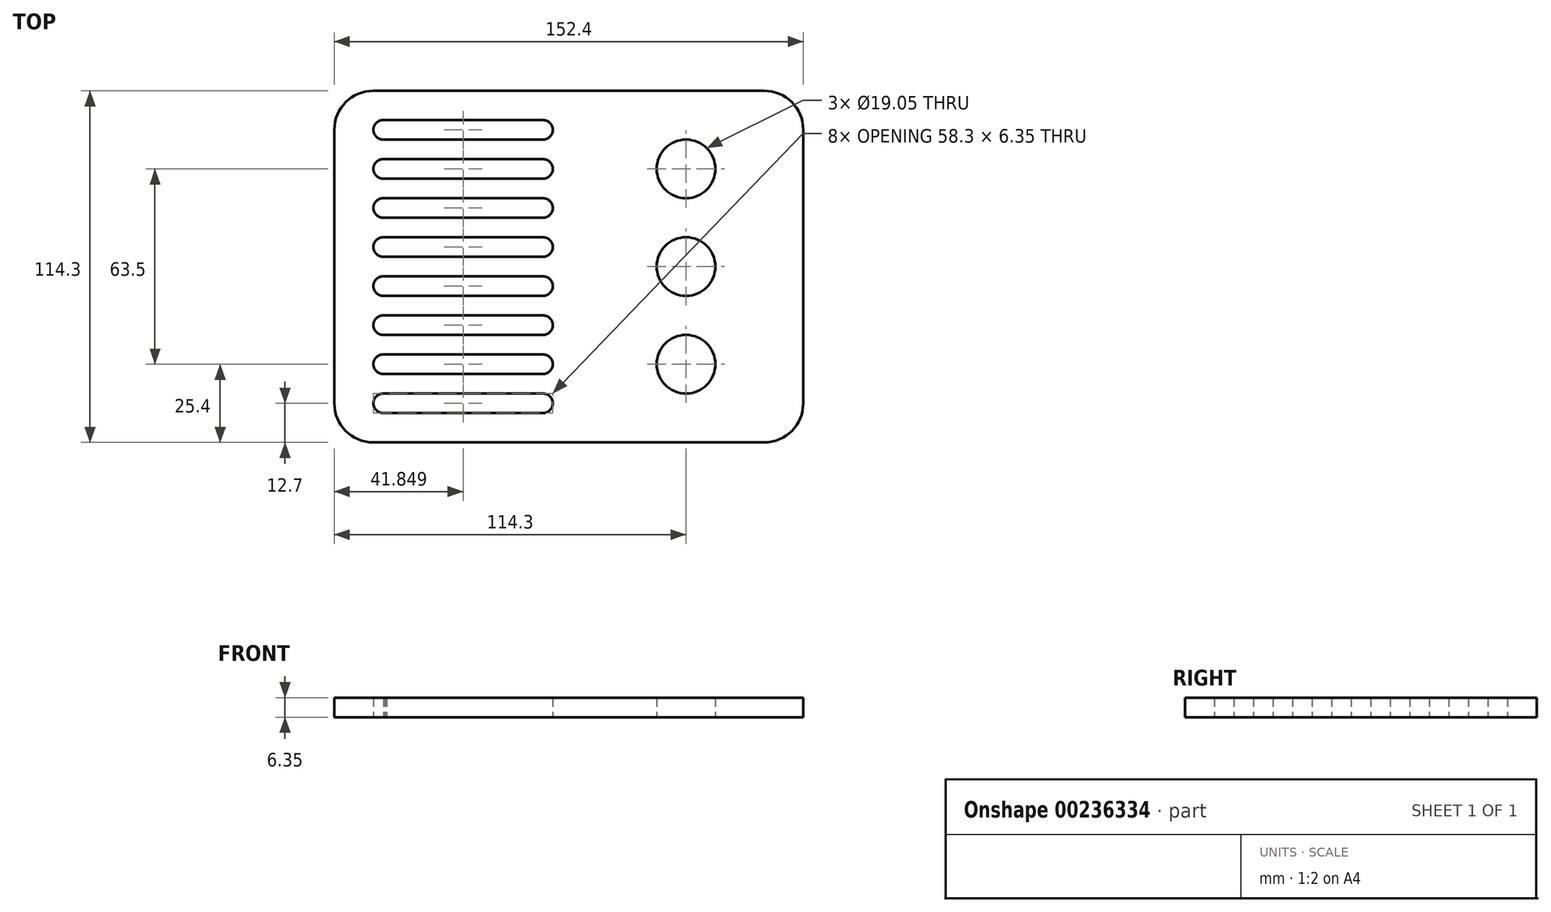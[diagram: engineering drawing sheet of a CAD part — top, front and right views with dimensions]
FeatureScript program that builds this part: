
annotation { "Feature Type Name" : "Feature", "Feature Type Description" : "" }
export const myFeature = defineFeature(function(context is Context, id is Id, definition is map)
    precondition{}
    {
        {
            var Q0;
            Q0=qCreatedBy(makeId("Top.planeOp"),FACE);
            var sketch = newSketch(context, id + "F0", { "sketchPlane" : qUnion([Q0])});
            skLineSegment(sketch, "E0.bottom", {"start": v(76.2, -57.15) * mm, "end": v(-76.2, -57.15) * mm});
            skLineSegment(sketch, "E0.top", {"start": v(76.2, 57.15) * mm, "end": v(-76.2, 57.15) * mm});
            skLineSegment(sketch, "E0.left", {"start": v(76.2, -57.15) * mm, "end": v(76.2, 57.15) * mm});
            skLineSegment(sketch, "E0.right", {"start": v(-76.2, -57.15) * mm, "end": v(-76.2, 57.15) * mm});
            skPoint(sketch, "E0.middle", {"position": v(0, 0) * mm});
            skCircle(sketch, "E1", {"center": v(38.1, -31.75) * mm, "radius": 9.53 * mm});
            skCircle(sketch, "E2", {"center": v(38.1, 0) * mm, "radius": 9.53 * mm});
            skCircle(sketch, "E3", {"center": v(38.1, 31.75) * mm, "radius": 9.53 * mm});
            skArc(sketch, "E4", {"start": v(-9.4, 41.28) * mm, "mid": v(-6.22, 44.45) * mm, "end": v(-9.4, 47.63) * mm});
            skLineSegment(sketch, "E5", {"start": v(-9.4, 47.63) * mm, "end": v(-60.32, 47.63) * mm});
            skLineSegment(sketch, "E6", {"start": v(-9.4, 41.28) * mm, "end": v(-60.2, 41.28) * mm});
            skArc(sketch, "E7", {"start": v(-60.32, 47.63) * mm, "mid": v(-63.5, 44.38) * mm, "end": v(-60.2, 41.28) * mm});
            skLineSegment(sketch, "E8.0.1.0", {"start": v(-9.4, 28.58) * mm, "end": v(-60.2, 28.58) * mm});
            skArc(sketch, "E8.0.1.1", {"start": v(-60.32, 34.93) * mm, "mid": v(-63.5, 31.68) * mm, "end": v(-60.2, 28.58) * mm});
            skLineSegment(sketch, "E8.0.1.2", {"start": v(-9.4, 34.93) * mm, "end": v(-60.32, 34.93) * mm});
            skArc(sketch, "E8.0.1.3", {"start": v(-9.4, 28.58) * mm, "mid": v(-6.22, 31.75) * mm, "end": v(-9.4, 34.93) * mm});
            skLineSegment(sketch, "E8.0.2.0", {"start": v(-9.4, 15.88) * mm, "end": v(-60.2, 15.88) * mm});
            skArc(sketch, "E8.0.2.1", {"start": v(-60.32, 22.23) * mm, "mid": v(-63.5, 18.98) * mm, "end": v(-60.2, 15.88) * mm});
            skLineSegment(sketch, "E8.0.2.2", {"start": v(-9.4, 22.23) * mm, "end": v(-60.32, 22.23) * mm});
            skArc(sketch, "E8.0.2.3", {"start": v(-9.4, 15.88) * mm, "mid": v(-6.22, 19.05) * mm, "end": v(-9.4, 22.23) * mm});
            skLineSegment(sketch, "E8.0.3.0", {"start": v(-9.4, 3.18) * mm, "end": v(-60.2, 3.18) * mm});
            skArc(sketch, "E8.0.3.1", {"start": v(-60.32, 9.53) * mm, "mid": v(-63.5, 6.28) * mm, "end": v(-60.2, 3.18) * mm});
            skLineSegment(sketch, "E8.0.3.2", {"start": v(-9.4, 9.53) * mm, "end": v(-60.32, 9.53) * mm});
            skArc(sketch, "E8.0.3.3", {"start": v(-9.4, 3.18) * mm, "mid": v(-6.22, 6.35) * mm, "end": v(-9.4, 9.53) * mm});
            skLineSegment(sketch, "E8.0.4.0", {"start": v(-9.4, -9.52) * mm, "end": v(-60.2, -9.52) * mm});
            skArc(sketch, "E8.0.4.1", {"start": v(-60.32, -3.17) * mm, "mid": v(-63.5, -6.42) * mm, "end": v(-60.2, -9.52) * mm});
            skLineSegment(sketch, "E8.0.4.2", {"start": v(-9.4, -3.17) * mm, "end": v(-60.32, -3.17) * mm});
            skArc(sketch, "E8.0.4.3", {"start": v(-9.4, -9.52) * mm, "mid": v(-6.22, -6.35) * mm, "end": v(-9.4, -3.17) * mm});
            skLineSegment(sketch, "E8.0.5.0", {"start": v(-9.4, -22.22) * mm, "end": v(-60.2, -22.22) * mm});
            skArc(sketch, "E8.0.5.1", {"start": v(-60.32, -15.87) * mm, "mid": v(-63.5, -19.12) * mm, "end": v(-60.2, -22.22) * mm});
            skLineSegment(sketch, "E8.0.5.2", {"start": v(-9.4, -15.87) * mm, "end": v(-60.32, -15.87) * mm});
            skArc(sketch, "E8.0.5.3", {"start": v(-9.4, -22.22) * mm, "mid": v(-6.22, -19.05) * mm, "end": v(-9.4, -15.87) * mm});
            skLineSegment(sketch, "E8.0.6.0", {"start": v(-9.4, -34.92) * mm, "end": v(-60.2, -34.92) * mm});
            skArc(sketch, "E8.0.6.1", {"start": v(-60.32, -28.57) * mm, "mid": v(-63.5, -31.82) * mm, "end": v(-60.2, -34.92) * mm});
            skLineSegment(sketch, "E8.0.6.2", {"start": v(-9.4, -28.57) * mm, "end": v(-60.32, -28.57) * mm});
            skArc(sketch, "E8.0.6.3", {"start": v(-9.4, -34.92) * mm, "mid": v(-6.22, -31.75) * mm, "end": v(-9.4, -28.57) * mm});
            skLineSegment(sketch, "E8.0.7.0", {"start": v(-9.4, -47.62) * mm, "end": v(-60.2, -47.62) * mm});
            skArc(sketch, "E8.0.7.1", {"start": v(-60.32, -41.27) * mm, "mid": v(-63.5, -44.52) * mm, "end": v(-60.2, -47.62) * mm});
            skLineSegment(sketch, "E8.0.7.2", {"start": v(-9.4, -41.27) * mm, "end": v(-60.32, -41.27) * mm});
            skArc(sketch, "E8.0.7.3", {"start": v(-9.4, -47.62) * mm, "mid": v(-6.22, -44.45) * mm, "end": v(-9.4, -41.27) * mm});
            skLineSegment(sketch, "E8.1.0.0", {"start": v(-8.89, 41.28) * mm, "end": v(-59.69, 41.28) * mm});
            skArc(sketch, "E8.1.0.1", {"start": v(-59.82, 47.63) * mm, "mid": v(-63, 44.38) * mm, "end": v(-59.69, 41.28) * mm});
            skLineSegment(sketch, "E8.1.0.2", {"start": v(-8.89, 47.63) * mm, "end": v(-59.82, 47.63) * mm});
            skArc(sketch, "E8.1.0.3", {"start": v(-8.89, 41.28) * mm, "mid": v(-5.71, 44.45) * mm, "end": v(-8.89, 47.63) * mm});
            skLineSegment(sketch, "E8.1.1.0", {"start": v(-8.89, 28.58) * mm, "end": v(-59.69, 28.58) * mm});
            skArc(sketch, "E8.1.1.1", {"start": v(-59.82, 34.93) * mm, "mid": v(-63, 31.68) * mm, "end": v(-59.69, 28.58) * mm});
            skLineSegment(sketch, "E8.1.1.2", {"start": v(-8.89, 34.93) * mm, "end": v(-59.82, 34.93) * mm});
            skArc(sketch, "E8.1.1.3", {"start": v(-8.89, 28.58) * mm, "mid": v(-5.71, 31.75) * mm, "end": v(-8.89, 34.93) * mm});
            skLineSegment(sketch, "E8.1.2.0", {"start": v(-8.89, 15.88) * mm, "end": v(-59.69, 15.88) * mm});
            skArc(sketch, "E8.1.2.1", {"start": v(-59.82, 22.23) * mm, "mid": v(-63, 18.98) * mm, "end": v(-59.69, 15.88) * mm});
            skLineSegment(sketch, "E8.1.2.2", {"start": v(-8.89, 22.23) * mm, "end": v(-59.82, 22.23) * mm});
            skArc(sketch, "E8.1.2.3", {"start": v(-8.89, 15.88) * mm, "mid": v(-5.71, 19.05) * mm, "end": v(-8.89, 22.23) * mm});
            skLineSegment(sketch, "E8.1.3.0", {"start": v(-8.89, 3.18) * mm, "end": v(-59.69, 3.18) * mm});
            skArc(sketch, "E8.1.3.1", {"start": v(-59.82, 9.53) * mm, "mid": v(-63, 6.28) * mm, "end": v(-59.69, 3.18) * mm});
            skLineSegment(sketch, "E8.1.3.2", {"start": v(-8.89, 9.53) * mm, "end": v(-59.82, 9.53) * mm});
            skArc(sketch, "E8.1.3.3", {"start": v(-8.89, 3.18) * mm, "mid": v(-5.71, 6.35) * mm, "end": v(-8.89, 9.53) * mm});
            skLineSegment(sketch, "E8.1.4.0", {"start": v(-8.89, -9.52) * mm, "end": v(-59.69, -9.52) * mm});
            skArc(sketch, "E8.1.4.1", {"start": v(-59.82, -3.17) * mm, "mid": v(-63, -6.42) * mm, "end": v(-59.69, -9.52) * mm});
            skLineSegment(sketch, "E8.1.4.2", {"start": v(-8.89, -3.17) * mm, "end": v(-59.82, -3.17) * mm});
            skArc(sketch, "E8.1.4.3", {"start": v(-8.89, -9.52) * mm, "mid": v(-5.71, -6.35) * mm, "end": v(-8.89, -3.17) * mm});
            skLineSegment(sketch, "E8.1.5.0", {"start": v(-8.89, -22.22) * mm, "end": v(-59.69, -22.22) * mm});
            skArc(sketch, "E8.1.5.1", {"start": v(-59.82, -15.87) * mm, "mid": v(-63, -19.12) * mm, "end": v(-59.69, -22.22) * mm});
            skLineSegment(sketch, "E8.1.5.2", {"start": v(-8.89, -15.87) * mm, "end": v(-59.82, -15.87) * mm});
            skArc(sketch, "E8.1.5.3", {"start": v(-8.89, -22.22) * mm, "mid": v(-5.71, -19.05) * mm, "end": v(-8.89, -15.87) * mm});
            skLineSegment(sketch, "E8.1.6.0", {"start": v(-8.89, -34.92) * mm, "end": v(-59.69, -34.92) * mm});
            skArc(sketch, "E8.1.6.1", {"start": v(-59.82, -28.57) * mm, "mid": v(-63, -31.82) * mm, "end": v(-59.69, -34.92) * mm});
            skLineSegment(sketch, "E8.1.6.2", {"start": v(-8.89, -28.57) * mm, "end": v(-59.82, -28.57) * mm});
            skArc(sketch, "E8.1.6.3", {"start": v(-8.89, -34.92) * mm, "mid": v(-5.71, -31.75) * mm, "end": v(-8.89, -28.57) * mm});
            skLineSegment(sketch, "E8.1.7.0", {"start": v(-8.89, -47.62) * mm, "end": v(-59.69, -47.62) * mm});
            skArc(sketch, "E8.1.7.1", {"start": v(-59.82, -41.27) * mm, "mid": v(-63, -44.52) * mm, "end": v(-59.69, -47.62) * mm});
            skLineSegment(sketch, "E8.1.7.2", {"start": v(-8.89, -41.27) * mm, "end": v(-59.82, -41.27) * mm});
            skArc(sketch, "E8.1.7.3", {"start": v(-8.89, -47.62) * mm, "mid": v(-5.71, -44.45) * mm, "end": v(-8.89, -41.27) * mm});
            skLineSegment(sketch, "E8.2.0.0", {"start": v(-8.38, 41.28) * mm, "end": v(-59.18, 41.28) * mm});
            skArc(sketch, "E8.2.0.1", {"start": v(-59.3, 47.63) * mm, "mid": v(-62.48, 44.38) * mm, "end": v(-59.18, 41.28) * mm});
            skLineSegment(sketch, "E8.2.0.2", {"start": v(-8.38, 47.63) * mm, "end": v(-59.3, 47.63) * mm});
            skArc(sketch, "E8.2.0.3", {"start": v(-8.38, 41.28) * mm, "mid": v(-5.2, 44.45) * mm, "end": v(-8.38, 47.63) * mm});
            skLineSegment(sketch, "E8.2.1.0", {"start": v(-8.38, 28.58) * mm, "end": v(-59.18, 28.58) * mm});
            skArc(sketch, "E8.2.1.1", {"start": v(-59.3, 34.93) * mm, "mid": v(-62.48, 31.68) * mm, "end": v(-59.18, 28.58) * mm});
            skLineSegment(sketch, "E8.2.1.2", {"start": v(-8.38, 34.93) * mm, "end": v(-59.3, 34.93) * mm});
            skArc(sketch, "E8.2.1.3", {"start": v(-8.38, 28.58) * mm, "mid": v(-5.2, 31.75) * mm, "end": v(-8.38, 34.93) * mm});
            skLineSegment(sketch, "E8.2.2.0", {"start": v(-8.38, 15.88) * mm, "end": v(-59.18, 15.88) * mm});
            skArc(sketch, "E8.2.2.1", {"start": v(-59.3, 22.23) * mm, "mid": v(-62.48, 18.98) * mm, "end": v(-59.18, 15.88) * mm});
            skLineSegment(sketch, "E8.2.2.2", {"start": v(-8.38, 22.23) * mm, "end": v(-59.3, 22.23) * mm});
            skArc(sketch, "E8.2.2.3", {"start": v(-8.38, 15.88) * mm, "mid": v(-5.2, 19.05) * mm, "end": v(-8.38, 22.23) * mm});
            skLineSegment(sketch, "E8.2.3.0", {"start": v(-8.38, 3.18) * mm, "end": v(-59.18, 3.18) * mm});
            skArc(sketch, "E8.2.3.1", {"start": v(-59.3, 9.53) * mm, "mid": v(-62.48, 6.28) * mm, "end": v(-59.18, 3.18) * mm});
            skLineSegment(sketch, "E8.2.3.2", {"start": v(-8.38, 9.53) * mm, "end": v(-59.3, 9.53) * mm});
            skArc(sketch, "E8.2.3.3", {"start": v(-8.38, 3.18) * mm, "mid": v(-5.2, 6.35) * mm, "end": v(-8.38, 9.53) * mm});
            skLineSegment(sketch, "E8.2.4.0", {"start": v(-8.38, -9.52) * mm, "end": v(-59.18, -9.52) * mm});
            skArc(sketch, "E8.2.4.1", {"start": v(-59.3, -3.17) * mm, "mid": v(-62.48, -6.42) * mm, "end": v(-59.18, -9.52) * mm});
            skLineSegment(sketch, "E8.2.4.2", {"start": v(-8.38, -3.17) * mm, "end": v(-59.3, -3.17) * mm});
            skArc(sketch, "E8.2.4.3", {"start": v(-8.38, -9.52) * mm, "mid": v(-5.2, -6.35) * mm, "end": v(-8.38, -3.17) * mm});
            skLineSegment(sketch, "E8.2.5.0", {"start": v(-8.38, -22.22) * mm, "end": v(-59.18, -22.22) * mm});
            skArc(sketch, "E8.2.5.1", {"start": v(-59.3, -15.87) * mm, "mid": v(-62.48, -19.12) * mm, "end": v(-59.18, -22.22) * mm});
            skLineSegment(sketch, "E8.2.5.2", {"start": v(-8.38, -15.87) * mm, "end": v(-59.3, -15.87) * mm});
            skArc(sketch, "E8.2.5.3", {"start": v(-8.38, -22.22) * mm, "mid": v(-5.2, -19.05) * mm, "end": v(-8.38, -15.87) * mm});
            skLineSegment(sketch, "E8.2.6.0", {"start": v(-8.38, -34.92) * mm, "end": v(-59.18, -34.92) * mm});
            skArc(sketch, "E8.2.6.1", {"start": v(-59.3, -28.57) * mm, "mid": v(-62.48, -31.82) * mm, "end": v(-59.18, -34.92) * mm});
            skLineSegment(sketch, "E8.2.6.2", {"start": v(-8.38, -28.57) * mm, "end": v(-59.3, -28.57) * mm});
            skArc(sketch, "E8.2.6.3", {"start": v(-8.38, -34.92) * mm, "mid": v(-5.2, -31.75) * mm, "end": v(-8.38, -28.57) * mm});
            skLineSegment(sketch, "E8.2.7.0", {"start": v(-8.38, -47.62) * mm, "end": v(-59.18, -47.62) * mm});
            skArc(sketch, "E8.2.7.1", {"start": v(-59.3, -41.27) * mm, "mid": v(-62.48, -44.52) * mm, "end": v(-59.18, -47.62) * mm});
            skLineSegment(sketch, "E8.2.7.2", {"start": v(-8.38, -41.27) * mm, "end": v(-59.3, -41.27) * mm});
            skArc(sketch, "E8.2.7.3", {"start": v(-8.38, -47.62) * mm, "mid": v(-5.2, -44.45) * mm, "end": v(-8.38, -41.27) * mm});
            skLineSegment(sketch, "E8.direction1", {"start": v(-60.2, 41.28) * mm, "end": v(-59.69, 41.28) * mm, "construction": true});
            skLineSegment(sketch, "E8.direction2", {"start": v(-60.2, 41.28) * mm, "end": v(-60.2, 28.58) * mm, "construction": true});
            skSolve(sketch);
        }
        {
            var Q0;
            Q0 = qSketchRegion(id + "F0", true);
            extrude(context, id + "F1", {"entities" : qUnion([Q0]), "depth" : 6.35 * mm});
        }
        {
            var Q0;
            Q0=makeQuery(id+"F1.opExtrude","SWEPT_EDGE",EDGE,{"disambiguationData":[OSD([sQuery(id+"F0.wireOp",EDGE,"E0.top"),sQuery(id+"F0.wireOp",EDGE,"E0.right")])]});
            var Q1;
            Q1=makeQuery(id+"F1.opExtrude","SWEPT_EDGE",EDGE,{"disambiguationData":[OSD([sQuery(id+"F0.wireOp",EDGE,"E0.bottom"),sQuery(id+"F0.wireOp",EDGE,"E0.right")])]});
            var Q2;
            Q2=makeQuery(id+"F1.opExtrude","SWEPT_EDGE",EDGE,{"disambiguationData":[OSD([sQuery(id+"F0.wireOp",EDGE,"E0.top"),sQuery(id+"F0.wireOp",EDGE,"E0.left")])]});
            var Q3;
            Q3=makeQuery(id+"F1.opExtrude","SWEPT_EDGE",EDGE,{"disambiguationData":[OSD([sQuery(id+"F0.wireOp",EDGE,"E0.bottom"),sQuery(id+"F0.wireOp",EDGE,"E0.left")])]});
            fillet(context, id + "F2", {"entities" : qUnion([Q0, Q1, Q2, Q3]), "radius" : 12.7 * mm, "tangentPropagation" : true, "allowEdgeOverflow" : false});
        }
    });
